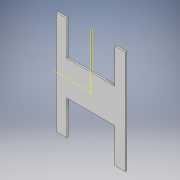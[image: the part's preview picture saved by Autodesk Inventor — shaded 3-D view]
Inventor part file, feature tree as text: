
AUTODESK INVENTOR PART (.ipt)
format: ipt  version: 2018 (Build 220112000, 112)  size: 121,856 bytes
history: native  units: mm
features: other x3, plane x2, mirror x2, extrude x1, pattern_circular x1, sketch x1
ambient origin geometry x8: Origin, YZ Plane, XZ Plane, XY Plane, X Axis, Y Axis, Z Axis, Center Point
bodies: Volumenkörper1 (feature_tree)
feature tree (10):
  other  "3D-Skizze1"
  extrude  "Extrusion1"  Depth=30.0mm
  plane  "Arbeitsebene1"
  plane  "Arbeitsebene2"
  mirror  "Spiegeln1"
  other  "Arbeitsachse1"
  pattern_circular  "Runde Anordnung1"  Count=15  [1 undecoded]
  mirror  "Spiegeln2"
  sketch  "Skizze1"  dims[d10=100.0mm d12=30.0mm d13=150.0mm d14=50.0mm d15=5.0mm d16=0.0mm d17=0.0mm d18=0.0mm d19=20.0mm d20=180.0deg]
  other  "Arbeitsachse2"
note: 1 required parameter value undecoded (feature->parameter linkage not recoverable at this tier; creation-order binding heuristic only, values carry confidence <= 0.55)
